# Revit family: LSS3838B5T-B.V2, B2T-B.V2
name_source: partatom
category: Plumbing Fixtures
units: mm (PartAtom-declared; Revit-internal decimal feet)

## family parameters
Always vertical = Yes
Cut with Voids When Loaded = No
OmniClass Number = 23.45.05.14.17
OmniClass Title = Showers
Part Type = Normal
Room Calculation Point = No
Round Connector Dimension = Use Diameter
Shared = No
Work Plane-Based = No

## types (2) — shared parameters
Assembly Code = D2010710
Description = Smooth Wall Finish, Traditional Bullnose Treshold
Keynote = 22 40 00.B3
Manufacturer = Best Bath Systems, Inc.
Type Comments = Barrier Free
URL = http://www.best-bath.com
Unit Depth = 39"
Unit Width = 38"

## per-type parameters (varying)
| type | Threshold Height | Unit Height |
| LSS3838B5T.V2 | 5/8" | 78 5/8" |
| LSS3838B2T.V2 | 2" | 79 3/4" |

note: column(s) folded — value = type name in every type: Model

## geometry (parser evidence)
native form markers: Blend x20, Sweep x2
no freeform markers — native parametric forms only
